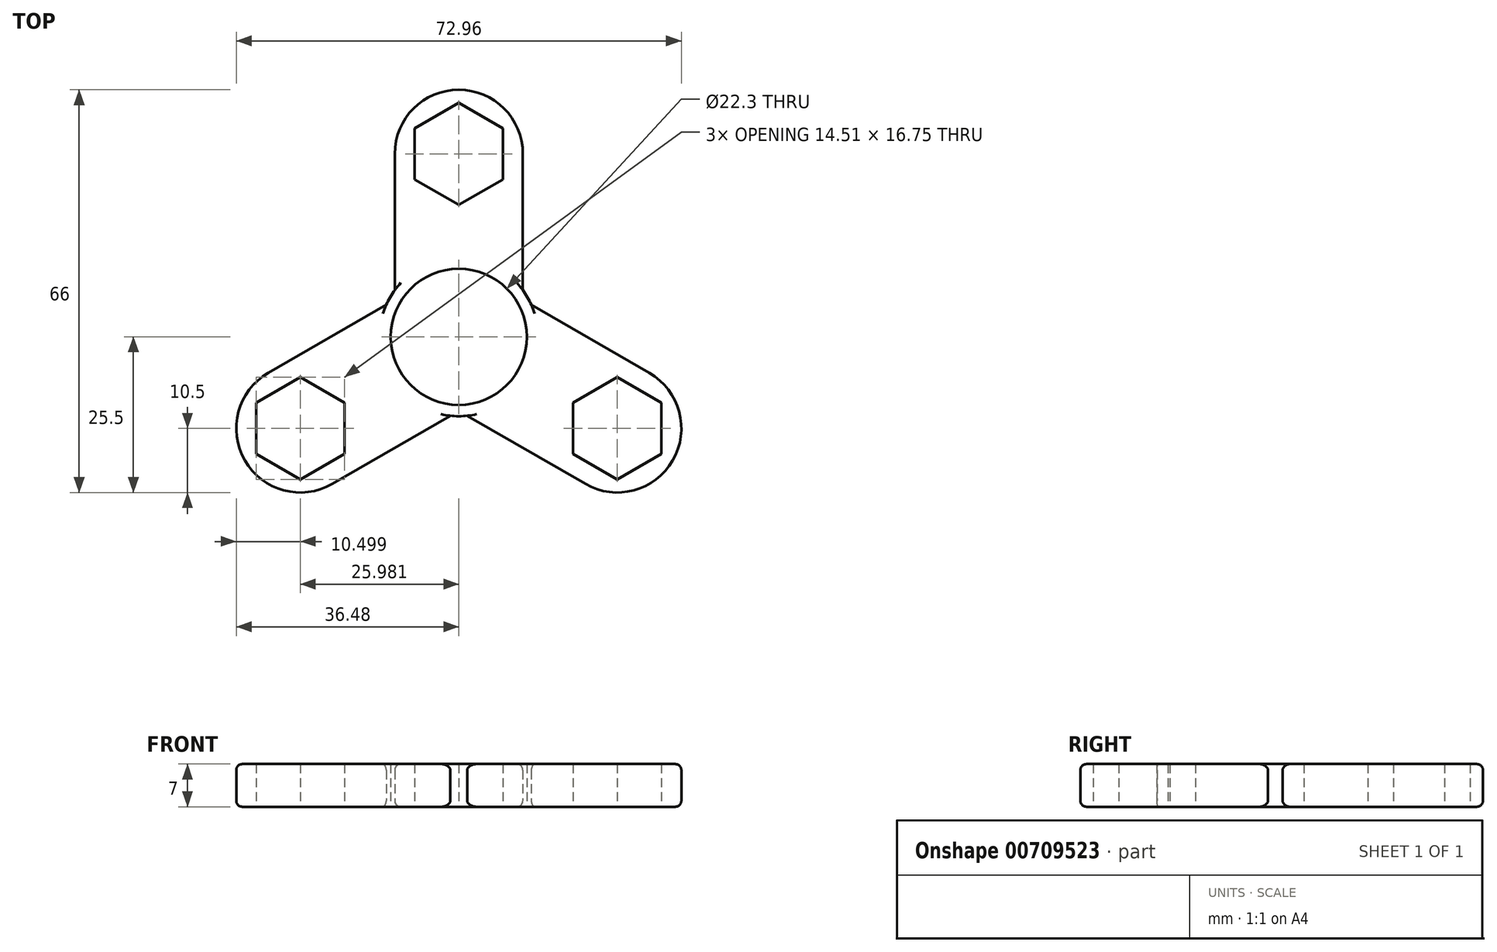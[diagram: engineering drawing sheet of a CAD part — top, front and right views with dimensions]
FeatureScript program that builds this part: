
annotation { "Feature Type Name" : "Feature", "Feature Type Description" : "" }
export const myFeature = defineFeature(function(context is Context, id is Id, definition is map)
    precondition{}
    {
        {
            var Q0;
            Q0=qCreatedBy(makeId("Top.planeOp"),FACE);
            var sketch = newSketch(context, id + "F0", { "sketchPlane" : qUnion([Q0])});
            skCircle(sketch, "E0", {"center": v(0, 0) * mm, "radius": 11.15 * mm});
            skCircle(sketch, "E1", {"center": v(0, 0) * mm, "radius": 13 * mm});
            skCircle(sketch, "E2.cCircle", {"center": v(0, 30) * mm, "radius": 7.25 * mm, "construction": true});
            skLineSegment(sketch, "E2.0", {"start": v(7.25, 34.19) * mm, "end": v(7.25, 25.81) * mm});
            skLineSegment(sketch, "E2.1", {"start": v(7.25, 25.81) * mm, "end": v(0, 21.62) * mm});
            skLineSegment(sketch, "E2.2", {"start": v(0, 21.62) * mm, "end": v(-7.25, 25.81) * mm});
            skLineSegment(sketch, "E2.3", {"start": v(-7.25, 25.81) * mm, "end": v(-7.25, 34.19) * mm});
            skLineSegment(sketch, "E2.4", {"start": v(-7.25, 34.19) * mm, "end": v(0, 38.38) * mm});
            skLineSegment(sketch, "E2.5", {"start": v(0, 38.38) * mm, "end": v(7.25, 34.19) * mm});
            skPoint(sketch, "E2.0.midPoint", {"position": v(7.25, 30) * mm});
            skCircle(sketch, "E3", {"center": v(0, 30) * mm, "radius": 10.5 * mm});
            skLineSegment(sketch, "E4", {"start": v(-10.5, 30) * mm, "end": v(-10.5, 7.66) * mm});
            skPoint(sketch, "E4.startSnap0", {"position": v(-7.25, 30) * mm});
            skLineSegment(sketch, "E5", {"start": v(10.5, 30) * mm, "end": v(10.5, 7.66) * mm});
            skLineSegment(sketch, "E6.1.0", {"start": v(-33.23, -19.19) * mm, "end": v(-33.23, -10.81) * mm});
            skLineSegment(sketch, "E6.1.2", {"start": v(-25.98, -23.37) * mm, "end": v(-33.23, -19.19) * mm});
            skLineSegment(sketch, "E6.1.3", {"start": v(-31.23, -5.9) * mm, "end": v(-11.89, 5.26) * mm});
            skPoint(sketch, "E6.1.4", {"position": v(-22.35, -21.28) * mm});
            skPoint(sketch, "E6.1.6", {"position": v(-29.6, -8.72) * mm});
            skCircle(sketch, "E6.1.7", {"center": v(-25.98, -15) * mm, "radius": 10.5 * mm});
            skLineSegment(sketch, "E6.1.8", {"start": v(-20.73, -24.1) * mm, "end": v(-1.39, -12.93) * mm});
            skLineSegment(sketch, "E6.1.9", {"start": v(-25.98, -6.62) * mm, "end": v(-18.73, -10.81) * mm});
            skCircle(sketch, "E6.1.10", {"center": v(-25.98, -15) * mm, "radius": 7.25 * mm, "construction": true});
            skLineSegment(sketch, "E6.1.11", {"start": v(-18.73, -10.81) * mm, "end": v(-18.73, -19.19) * mm});
            skLineSegment(sketch, "E6.1.12", {"start": v(-33.23, -10.81) * mm, "end": v(-25.98, -6.62) * mm});
            skLineSegment(sketch, "E6.1.13", {"start": v(-18.73, -19.19) * mm, "end": v(-25.98, -23.38) * mm});
            skLineSegment(sketch, "E6.2.0", {"start": v(33.23, -19.19) * mm, "end": v(25.98, -23.38) * mm});
            skLineSegment(sketch, "E6.2.2", {"start": v(33.23, -10.81) * mm, "end": v(33.23, -19.19) * mm});
            skLineSegment(sketch, "E6.2.3", {"start": v(20.73, -24.1) * mm, "end": v(1.39, -12.93) * mm});
            skPoint(sketch, "E6.2.4", {"position": v(29.6, -8.72) * mm});
            skPoint(sketch, "E6.2.6", {"position": v(22.35, -21.28) * mm});
            skCircle(sketch, "E6.2.7", {"center": v(25.98, -15) * mm, "radius": 10.5 * mm});
            skLineSegment(sketch, "E6.2.8", {"start": v(31.23, -5.9) * mm, "end": v(11.89, 5.26) * mm});
            skLineSegment(sketch, "E6.2.9", {"start": v(18.73, -19.19) * mm, "end": v(18.73, -10.81) * mm});
            skCircle(sketch, "E6.2.10", {"center": v(25.98, -15) * mm, "radius": 7.25 * mm, "construction": true});
            skLineSegment(sketch, "E6.2.11", {"start": v(18.73, -10.81) * mm, "end": v(25.98, -6.62) * mm});
            skLineSegment(sketch, "E6.2.12", {"start": v(25.98, -23.37) * mm, "end": v(18.73, -19.19) * mm});
            skLineSegment(sketch, "E6.2.13", {"start": v(25.98, -6.62) * mm, "end": v(33.23, -10.81) * mm});
            skSolve(sketch);
        }
        {
            var Q0;
            Q0 = qSketchRegion(id + "F0", true);
            extrude(context, id + "F1", {"entities" : qUnion([Q0]), "depth" : 7 * mm, "offsetDistance" : 25 * mm});
        }
        {
            var Q0;
            Q0=makeQuery(id+"F1.opExtrude","CAP_EDGE",EDGE,{"disambiguationData":[OSD([sQuery(id+"F0.wireOp",EDGE,"E6.1.3")])],"isStart":false});
            var Q1;
            Q1=makeQuery(id+"F1.opExtrude","CAP_EDGE",EDGE,{"disambiguationData":[OSD([sQuery(id+"F0.wireOp",EDGE,"E6.2.3")])],"isStart":false});
            var Q2;
            Q2=makeQuery(id+"F1.opExtrude","CAP_EDGE",EDGE,{"disambiguationData":[OSD([sQuery(id+"F0.wireOp",EDGE,"E6.2.8")])],"isStart":false});
            var Q3;
            Q3=makeQuery(id+"F1.opExtrude","CAP_EDGE",EDGE,{"disambiguationData":[OSD([sQuery(id+"F0.wireOp",EDGE,"E5")])],"isStart":false});
            var Q4;
            Q4=makeQuery(id+"F1.opExtrude","CAP_EDGE",EDGE,{"disambiguationData":[OSD([sQuery(id+"F0.wireOp",EDGE,"E4")])],"isStart":false});
            var Q5;
            Q5=makeQuery(id+"F1.opExtrude","CAP_EDGE",EDGE,{"disambiguationData":[OSD([sQuery(id+"F0.wireOp",EDGE,"E6.1.8")])],"isStart":false});
            var Q6;
            Q6=makeQuery(id+"F1.opExtrude","CAP_EDGE",EDGE,{"disambiguationData":[OSD([sQuery(id+"F0.wireOp",EDGE,"E6.2.3")])],"isStart":true});
            var Q7;
            Q7=makeQuery(id+"F1.opExtrude","CAP_EDGE",EDGE,{"disambiguationData":[OSD([sQuery(id+"F0.wireOp",EDGE,"E6.1.8")])],"isStart":true});
            var Q8;
            Q8=makeQuery(id+"F1.opExtrude","CAP_EDGE",EDGE,{"disambiguationData":[OSD([sQuery(id+"F0.wireOp",EDGE,"E4")])],"isStart":true});
            fillet(context, id + "F2", {"entities" : qUnion([Q0, Q1, Q2, Q3, Q4, Q5, Q6, Q7, Q8]), "radius" : 1 * mm, "tangentPropagation" : true, "allowEdgeOverflow" : false});
        }
    });
